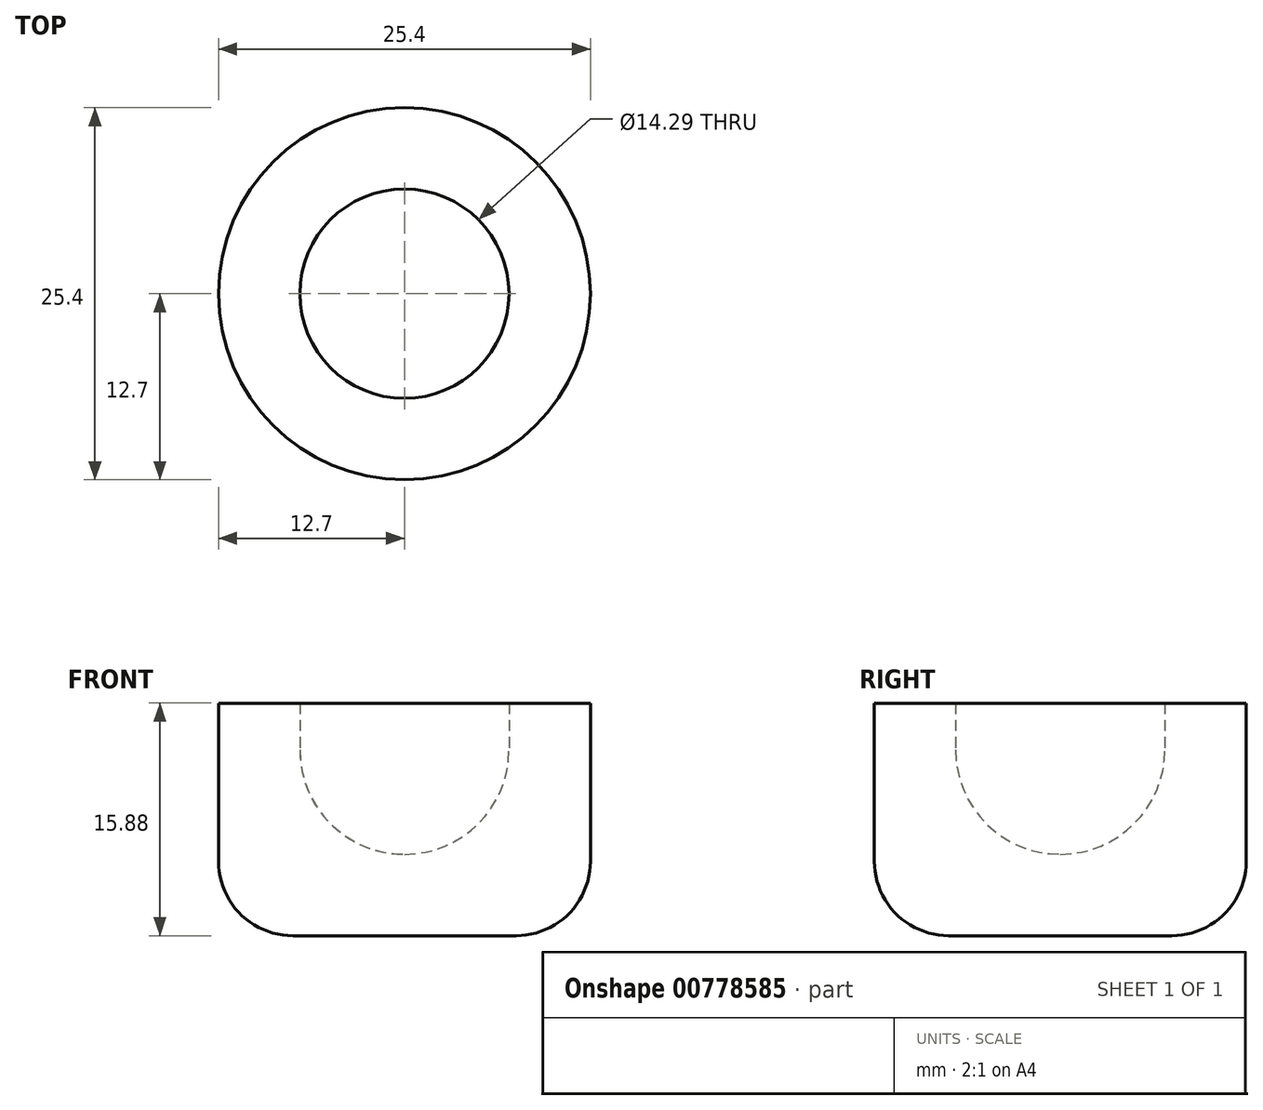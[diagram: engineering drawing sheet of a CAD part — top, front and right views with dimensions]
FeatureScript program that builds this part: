
annotation { "Feature Type Name" : "Feature", "Feature Type Description" : "" }
export const myFeature = defineFeature(function(context is Context, id is Id, definition is map)
    precondition{}
    {
        {
            var Q0;
            Q0=qCreatedBy(makeId("Front.planeOp"),FACE);
            var sketch = newSketch(context, id + "F0", { "sketchPlane" : qUnion([Q0])});
            skLineSegment(sketch, "E0.bottom", {"start": v(0, 0) * mm, "end": v(12.7, 0) * mm});
            skLineSegment(sketch, "E0.top", {"start": v(7.14, 15.88) * mm, "end": v(12.7, 15.88) * mm});
            skLineSegment(sketch, "E0.left", {"start": v(0, 0) * mm, "end": v(0, 5.56) * mm});
            skLineSegment(sketch, "E0.right", {"start": v(12.7, 0) * mm, "end": v(12.7, 15.88) * mm});
            skArc(sketch, "E1", {"start": v(0, 5.56) * mm, "mid": v(5.05, 7.65) * mm, "end": v(7.14, 12.7) * mm});
            skLineSegment(sketch, "E2", {"start": v(7.14, 12.7) * mm, "end": v(7.14, 15.88) * mm});
            skSolve(sketch);
        }
        {
            var Q0;
            Q0=makeQuery(id+"F0.imprint","IMPRINT",FACE,{"disambiguationData":[TD([[makeQuery(id+"F0.imprint","IMPRINT",EDGE,{"derivedFrom":sQuery(id+"F0.wireOp",EDGE,"E0.bottom")}),1.0]])]});
            var Q1;
            Q1=sQuery(id+"F0.wireOp",EDGE,"E0.left");
            revolve(context, id + "F1", {"surfaceOperationType" : NewSurfaceOperationType.NEW, "entities" : qUnion([Q0]), "axis" : qUnion([Q1]), "revolveType" : RevolveType.FULL});
        }
        {
            var Q0;
            Q0=makeQuery(id+"F1.opRevolve","SWEPT_EDGE",EDGE,{"disambiguationData":[OSD([sQuery(id+"F0.wireOp",EDGE,"E0.bottom"),sQuery(id+"F0.wireOp",EDGE,"E0.right")])]});
            fillet(context, id + "F2", {"entities" : qUnion([Q0]), "radius" : 5.08 * mm, "tangentPropagation" : true, "allowEdgeOverflow" : false});
        }
    });
